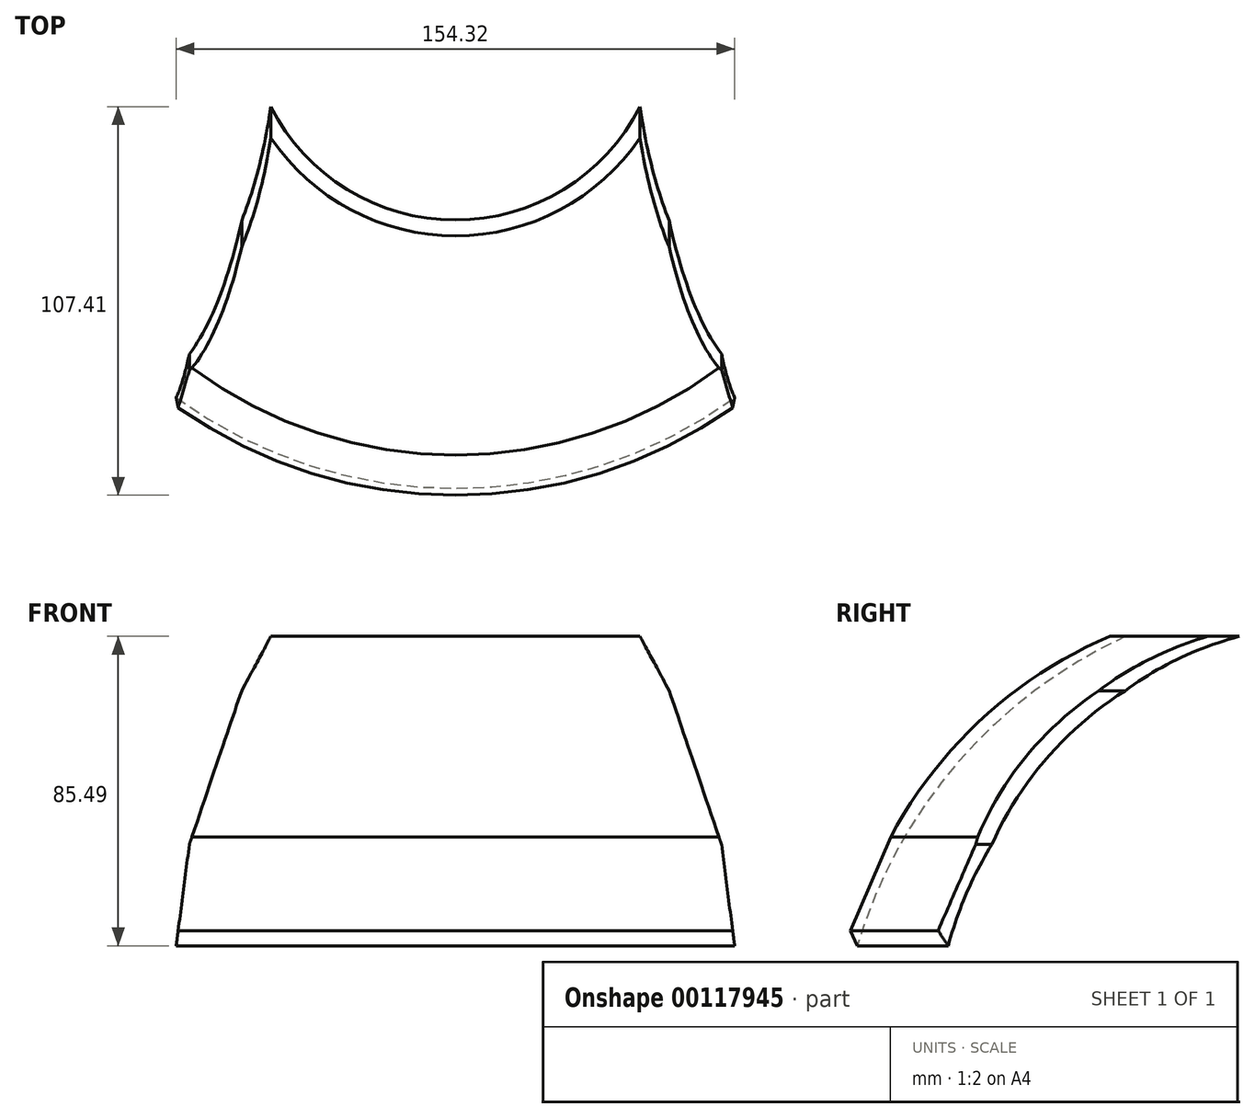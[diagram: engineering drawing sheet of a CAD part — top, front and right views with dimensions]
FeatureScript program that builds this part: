
annotation { "Feature Type Name" : "Feature", "Feature Type Description" : "" }
export const myFeature = defineFeature(function(context is Context, id is Id, definition is map)
    precondition{}
    {
        {
            var Q0;
            Q0=qCreatedBy(makeId("Front.planeOp"),FACE);
            var sketch = newSketch(context, id + "F0", { "sketchPlane" : qUnion([Q0])});
            skCircle(sketch, "E0", {"center": v(0, 0) * mm, "radius": 137 * mm});
            skLineSegment(sketch, "E1", {"start": v(0, 0) * mm, "end": v(251.53, 0) * mm, "construction": true});
            skLineSegment(sketch, "E2", {"start": v(0, 32) * mm, "end": v(251.53, 32) * mm, "construction": true});
            skLineSegment(sketch, "E3", {"start": v(0, 74.5) * mm, "end": v(251.53, 74.5) * mm, "construction": true});
            skLineSegment(sketch, "E4", {"start": v(114.97, 74.5) * mm, "end": v(-114.97, 74.5) * mm});
            skLineSegment(sketch, "E5", {"start": v(133.21, 32) * mm, "end": v(-133.21, 32) * mm});
            skPoint(sketch, "E5.startSnap0", {"position": v(125.77, 32) * mm});
            skLineSegment(sketch, "E6", {"start": v(114.97, 74.5) * mm, "end": v(133.21, 32) * mm});
            skLineSegment(sketch, "E7", {"start": v(-114.97, 74.5) * mm, "end": v(-133.21, 32) * mm});
            skLineSegment(sketch, "E8", {"start": v(-130.75, 37.74) * mm, "end": v(-133.25, 43.2) * mm});
            skLineSegment(sketch, "E9", {"start": v(-133.25, 43.2) * mm, "end": v(-122.13, 69.1) * mm});
            skArc(sketch, "E10", {"start": v(-48.83, 129.1) * mm, "mid": v(-91.47, 106.43) * mm, "end": v(-122.13, 69.1) * mm});
            skLineSegment(sketch, "E11", {"start": v(-48.83, 129.1) * mm, "end": v(-45.84, 129.1) * mm});
            skLineSegment(sketch, "E12", {"start": v(0, 32) * mm, "end": v(0, 137) * mm, "construction": true});
            skLineSegment(sketch, "E13", {"start": v(-26.7, 134.37) * mm, "end": v(-26.7, 142.46) * mm});
            skLineSegment(sketch, "E14", {"start": v(-26.7, 142.46) * mm, "end": v(-202.44, 142.46) * mm});
            skLineSegment(sketch, "E15", {"start": v(-202.44, 142.46) * mm, "end": v(-200.7, 13.24) * mm});
            skLineSegment(sketch, "E16", {"start": v(-200.7, 13.24) * mm, "end": v(-136.36, 13.24) * mm});
            skSolve(sketch);
        }
        {
            var Q0;
            Q0=qCreatedBy(makeId("Front.planeOp"),FACE);
            cPlane(context, id + "F1", {"entities" : qUnion([Q0]), "cplaneType" : CPlaneType.OFFSET, "offset" : 300 * mm, "width" : 150 * mm, "height" : 150 * mm});
        }
        {
            var Q0;
            Q0=qCreatedBy(id+"F1.planeOp",FACE);
            var sketch = newSketch(context, id + "F2", { "sketchPlane" : qUnion([Q0])});
            skLineSegment(sketch, "E17", {"start": v(0, 137) * mm, "end": v(-257.89, 137) * mm, "construction": true});
            skLineSegment(sketch, "E18", {"start": v(0, 124.5) * mm, "end": v(-51, 124.5) * mm});
            skLineSegment(sketch, "E19", {"start": v(0, 32) * mm, "end": v(-250.77, 32) * mm, "construction": true});
            skLineSegment(sketch, "E20", {"start": v(0, 32) * mm, "end": v(-78.07, 32) * mm});
            skLineSegment(sketch, "E21", {"start": v(-78.07, 32) * mm, "end": v(-73.52, 67) * mm});
            skLineSegment(sketch, "E22", {"start": v(-73.52, 67) * mm, "end": v(0, 67) * mm, "construction": true});
            skLineSegment(sketch, "E23", {"start": v(-73.52, 67) * mm, "end": v(-59.06, 109.5) * mm});
            skLineSegment(sketch, "E24", {"start": v(-59.06, 109.5) * mm, "end": v(0, 109.5) * mm, "construction": true});
            skLineSegment(sketch, "E25", {"start": v(-51, 124.5) * mm, "end": v(-59.06, 109.5) * mm});
            skLineSegment(sketch, "E26.MirrorCS", {"start": v(0, 124.5) * mm, "end": v(51, 124.5) * mm});
            skLineSegment(sketch, "E27.MirrorCS", {"start": v(51, 124.5) * mm, "end": v(59.06, 109.5) * mm});
            skLineSegment(sketch, "E28.MirrorCS", {"start": v(73.52, 67) * mm, "end": v(59.06, 109.5) * mm});
            skLineSegment(sketch, "E29.MirrorCS", {"start": v(78.07, 32) * mm, "end": v(73.52, 67) * mm});
            skLineSegment(sketch, "E30.MirrorCS", {"start": v(0, 32) * mm, "end": v(250.77, 32) * mm, "construction": true});
            skLineSegment(sketch, "E31", {"start": v(0, 32) * mm, "end": v(78.07, 32) * mm});
            skSolve(sketch);
        }
        {
            var Q0;
            Q0=makeQuery(id+"F2.imprint","IMPRINT",FACE,{"disambiguationData":[TD([[makeQuery(id+"F2.imprint","IMPRINT",EDGE,{"derivedFrom":sQuery(id+"F2.wireOp",EDGE,"E18")}),1.0]])]});
            extrude(context, id + "F3", {"entities" : qUnion([Q0]), "oppositeDirection" : true, "depth" : 289.3 * mm});
        }
        {
            var Q0;
            {var subQ0=sQuery(id+"F0.wireOp",EDGE,"E9");Q0=makeQuery(id+"F0.imprint","IMPRINT",FACE,{"disambiguationData":[TD([[makeQuery(id+"F0.imprint","IMPRINT",EDGE,{"derivedFrom":subQ0}),-1.0]])]});}
            var Q1;
            Q1=sQuery(id+"F0.wireOp",EDGE,"E12");
            revolve(context, id + "F4", {"operationType" : NewBodyOperationType.INTERSECT, "entities" : qUnion([Q0]), "axis" : qUnion([Q1]), "revolveType" : RevolveType.FULL, "oppositeDirection" : true});
        }
    });
